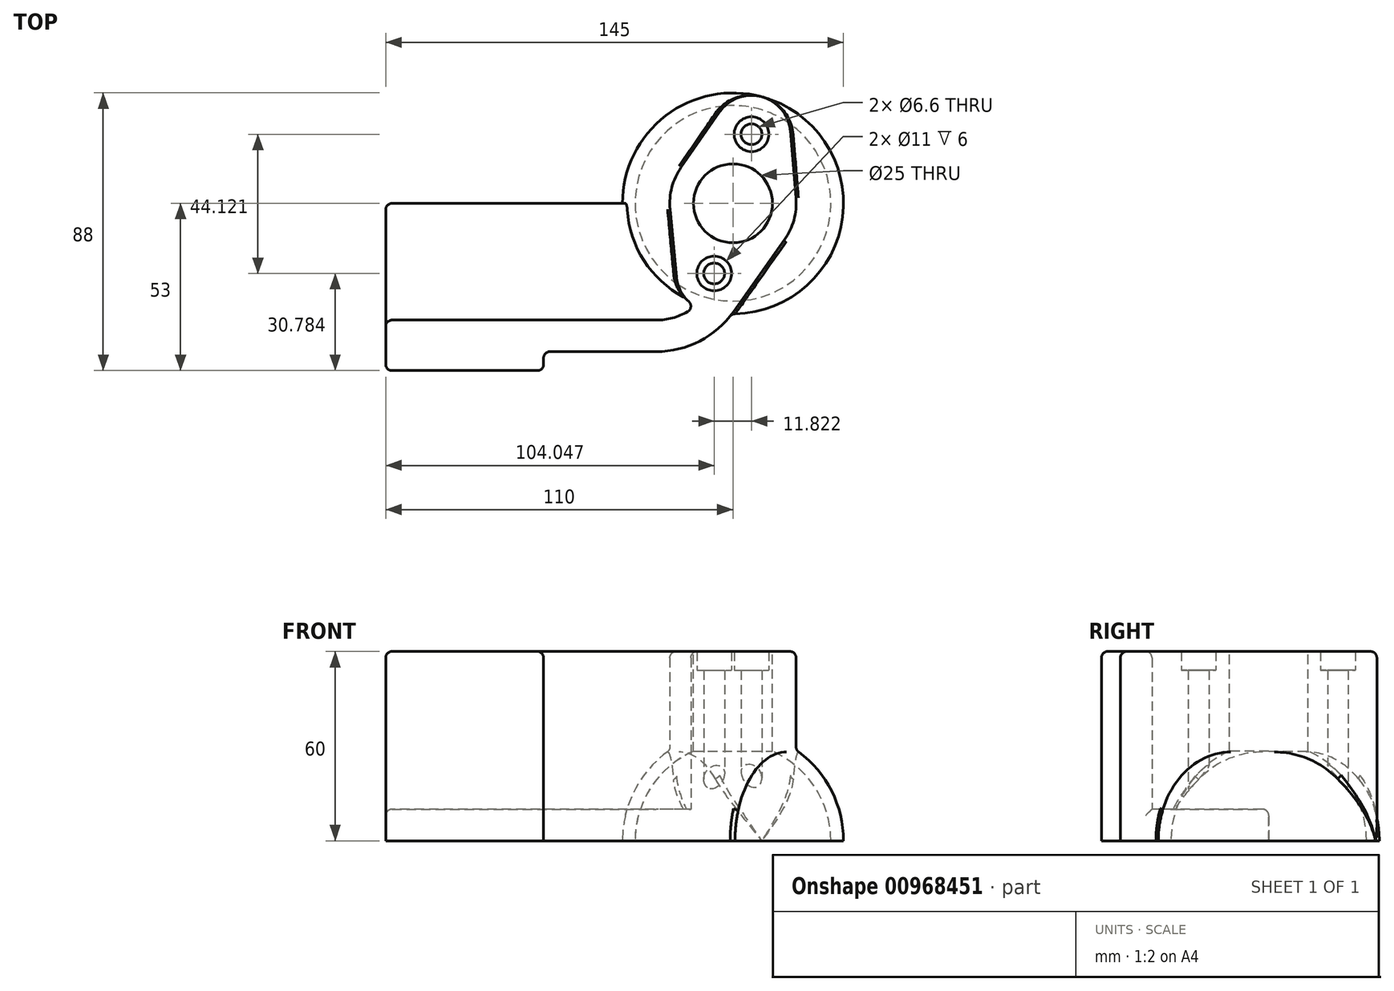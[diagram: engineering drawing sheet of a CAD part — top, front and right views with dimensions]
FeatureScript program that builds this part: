
annotation { "Feature Type Name" : "Feature", "Feature Type Description" : "" }
export const myFeature = defineFeature(function(context is Context, id is Id, definition is map)
    precondition{}
    {
        {
            var Q0;
            Q0=qCreatedBy(makeId("Top.planeOp"),FACE);
            var sketch = newSketch(context, id + "F0", { "sketchPlane" : qUnion([Q0])});
            skArc(sketch, "E0", {"start": v(-0.32, -35) * mm, "mid": v(6.97, 34.3) * mm, "end": v(-13.36, -32.35) * mm});
            skCircle(sketch, "E1", {"center": v(0, 0) * mm, "radius": 12.5 * mm, "construction": true});
            skLineSegment(sketch, "E2", {"start": v(9.06, 33.8) * mm, "end": v(-9.06, -33.8) * mm, "construction": true});
            skArc(sketch, "E3", {"start": v(-16.43, 11.41) * mm, "mid": v(-19.34, 5.08) * mm, "end": v(-19.91, -1.87) * mm});
            skArc(sketch, "E4", {"start": v(-17.9, -23.34) * mm, "mid": v(-16.68, -27.6) * mm, "end": v(-14, -31.12) * mm});
            skLineSegment(sketch, "E5", {"start": v(-4.25, 28.94) * mm, "end": v(-16.43, 11.41) * mm});
            skLineSegment(sketch, "E6", {"start": v(18.15, 22.93) * mm, "end": v(19.93, 1.67) * mm});
            skLineSegment(sketch, "E7", {"start": v(-17.9, -23.34) * mm, "end": v(-19.91, -1.87) * mm});
            skLineSegment(sketch, "E8", {"start": v(0.15, -34.36) * mm, "end": v(16.31, -11.57) * mm});
            skArc(sketch, "E9.trimOffspring", {"start": v(18.15, 22.93) * mm, "mid": v(9.06, 33.8) * mm, "end": v(-4.25, 28.94) * mm});
            skArc(sketch, "E10.trimOffspring", {"start": v(16.31, -11.57) * mm, "mid": v(19.3, -5.27) * mm, "end": v(19.93, 1.67) * mm});
            skPoint(sketch, "E11.orphan", {"position": v(20.07, 0) * mm});
            skPoint(sketch, "E12.orphan", {"position": v(-20.09, 0) * mm});
            skLineSegment(sketch, "E13", {"start": v(-34.3, -7) * mm, "end": v(-110, -7) * mm});
            skLineSegment(sketch, "E14", {"start": v(-110, -7) * mm, "end": v(-110, -53) * mm});
            skLineSegment(sketch, "E15", {"start": v(-110, -53) * mm, "end": v(-60, -53) * mm});
            skLineSegment(sketch, "E16", {"start": v(-60, -53) * mm, "end": v(-60, -47) * mm});
            skLineSegment(sketch, "E17", {"start": v(-60, -47) * mm, "end": v(-24.32, -47) * mm});
            skLineSegment(sketch, "E18", {"start": v(-110, -37) * mm, "end": v(-24.32, -37) * mm});
            skArc(sketch, "E19.filletArc", {"start": v(-24.32, -47) * mm, "mid": v(-10.55, -43.65) * mm, "end": v(0.15, -34.36) * mm});
            skArc(sketch, "E20", {"start": v(-24.32, -37) * mm, "mid": v(-19.16, -36.32) * mm, "end": v(-14.35, -34.33) * mm});
            skArc(sketch, "E21.filletArc", {"start": v(-14.35, -34.33) * mm, "mid": v(-13.35, -32.81) * mm, "end": v(-14, -31.12) * mm});
            skSolve(sketch);
        }
        {
            var Q0;
            Q0=qCreatedBy(makeId("Front.planeOp"),FACE);
            var sketch = newSketch(context, id + "F1", { "sketchPlane" : qUnion([Q0])});
            skArc(sketch, "E22", {"start": v(35, 0) * mm, "mid": v(24.75, 24.75) * mm, "end": v(0, 35) * mm});
            skPoint(sketch, "E23.orphan", {"position": v(0, 35) * mm});
            skLineSegment(sketch, "E24", {"start": v(0, 35) * mm, "end": v(0, 0) * mm});
            skLineSegment(sketch, "E25", {"start": v(0, 0) * mm, "end": v(35, 0) * mm});
            skSolve(sketch);
        }
        {
            var Q0;
            Q0=makeQuery(id+"F0.imprint","IMPRINT",FACE,{"disambiguationData":[TD([[makeQuery(id+"F0.imprint","IMPRINT",EDGE,{"derivedFrom":sQuery(id+"F0.wireOp",EDGE,"E3")}),1.0]])]});
            extrude(context, id + "F2", {"entities" : qUnion([Q0]), "depth" : 60 * mm, "offsetDistance" : 25 * mm});
        }
        {
            var Q0;
            Q0=makeQuery(id+"F1.imprint","IMPRINT",FACE,{"disambiguationData":[TD([[makeQuery(id+"F1.imprint","IMPRINT",EDGE,{"derivedFrom":sQuery(id+"F1.wireOp",EDGE,"E22")}),1.0]])]});
            var Q1;
            Q1=sQuery(id+"F1.wireOp",EDGE,"E24");
            revolve(context, id + "F3", {"operationType" : NewBodyOperationType.ADD, "surfaceOperationType" : NewSurfaceOperationType.NEW, "entities" : qUnion([Q0]), "axis" : qUnion([Q1]), "revolveType" : RevolveType.FULL});
        }
        {
            var Q0;
            Q0=makeQuery(id+"F2.opExtrude","SWEPT_FACE",FACE,{"disambiguationData":[OSD([sQuery(id+"F0.wireOp",EDGE,"E18")])]});
            var sketch = newSketch(context, id + "F4", { "sketchPlane" : qUnion([Q0])});
            skLineSegment(sketch, "E26.bottom", {"start": v(110, 0) * mm, "end": v(1.96, 0) * mm});
            skLineSegment(sketch, "E26.top", {"start": v(110, 10) * mm, "end": v(1.96, 10) * mm});
            skLineSegment(sketch, "E26.left", {"start": v(110, 0) * mm, "end": v(110, 10) * mm});
            skLineSegment(sketch, "E26.right", {"start": v(1.96, 0) * mm, "end": v(1.96, 10) * mm});
            skSolve(sketch);
        }
        {
            var Q0;
            Q0 = qSketchRegion(id + "F4", true);
            var Q1;
            Q1=qCreatedBy(makeId("Front.planeOp"),FACE);
            extrude(context, id + "F5", {"entities" : qUnion([Q0]), "operationType" : NewBodyOperationType.ADD, "endBound" : BoundingType.UP_TO_SURFACE, "depth" : 25 * mm, "endBoundEntityFace" : qUnion([Q1]), "offsetDistance" : 25 * mm});
        }
        {
            var Q0;
            Q0=makeQuery(id+"F3.boolean.opBoolean","INTERSECT",EDGE,{"derivedFrom":[makeQuery(id+"F2.opExtrude","SWEPT_FACE",FACE,{"disambiguationData":[OSD([sQuery(id+"F0.wireOp",EDGE,"E8")])]}),makeQuery(id+"F3.opRevolve","SWEPT_FACE",FACE,{"disambiguationData":[OSD([sQuery(id+"F1.wireOp",EDGE,"E22")])]})]});
            var Q1;
            Q1=makeQuery(id+"F3.boolean.opBoolean","INTERSECT",EDGE,{"derivedFrom":[makeQuery(id+"F2.opExtrude","SWEPT_FACE",FACE,{"disambiguationData":[OSD([sQuery(id+"F0.wireOp",EDGE,"E5")])]}),makeQuery(id+"F3.opRevolve","SWEPT_FACE",FACE,{"disambiguationData":[OSD([sQuery(id+"F1.wireOp",EDGE,"E22")])]})]});
            var Q2;
            Q2=makeQuery(id+"F5.opExtrude","CAP_EDGE",EDGE,{"disambiguationData":[OSD([sQuery(id+"F4.wireOp",EDGE,"E26.top")])],"isStart":false});
            var Q3;
            Q3=makeQuery(id+"F2.opExtrude","SWEPT_EDGE",EDGE,{"disambiguationData":[OSD([sQuery(id+"F0.wireOp",EDGE,"E16"),sQuery(id+"F0.wireOp",EDGE,"E17")])]});
            var Q4;
            Q4=makeQuery(id+"F2.opExtrude","SWEPT_EDGE",EDGE,{"disambiguationData":[OSD([sQuery(id+"F0.wireOp",EDGE,"E15"),sQuery(id+"F0.wireOp",EDGE,"E16")])]});
            var Q5;
            Q5=makeQuery(id+"F2.opExtrude","SWEPT_EDGE",EDGE,{"disambiguationData":[OSD([sQuery(id+"F0.wireOp",EDGE,"E14"),sQuery(id+"F0.wireOp",EDGE,"E15")])]});
            var Q6;
            Q6=makeQuery(id+"F2.opExtrude","SWEPT_EDGE",EDGE,{"disambiguationData":[OSD([sQuery(id+"F0.wireOp",EDGE,"E14"),sQuery(id+"F0.wireOp",EDGE,"E18")])]});
            fillet(context, id + "F6", {"entities" : qUnion([Q0, Q1, Q2, Q3, Q4, Q5, Q6]), "radius" : 2 * mm, "tangentPropagation" : true, "allowEdgeOverflow" : false});
        }
        {
            var Q0;
            Q0=makeQuery(id+"F5.opExtrude","SWEPT_EDGE",EDGE,{"disambiguationData":[OSD([sQuery(id+"F0.wireOp",EDGE,"E14"),sQuery(id+"F0.wireOp",EDGE,"E18"),sQuery(id+"F4.wireOp",EDGE,"E26.top"),sQuery(id+"F4.wireOp",EDGE,"E26.left")])]});
            fillet(context, id + "F7", {"entities" : qUnion([Q0]), "radius" : 2 * mm, "tangentPropagation" : true, "allowEdgeOverflow" : false});
        }
        {
            var Q0;
            Q0=makeQuery(id+"F2.opExtrude","CAP_FACE",FACE,{"disambiguationData":[OSD([sQuery(id+"F0.wireOp",EDGE,"E3"),sQuery(id+"F0.wireOp",EDGE,"E4"),sQuery(id+"F0.wireOp",EDGE,"E5"),sQuery(id+"F0.wireOp",EDGE,"E6"),sQuery(id+"F0.wireOp",EDGE,"E7"),sQuery(id+"F0.wireOp",EDGE,"E8"),sQuery(id+"F0.wireOp",EDGE,"E9.trimOffspring"),sQuery(id+"F0.wireOp",EDGE,"E10.trimOffspring"),sQuery(id+"F0.wireOp",EDGE,"E14"),sQuery(id+"F0.wireOp",EDGE,"E15"),sQuery(id+"F0.wireOp",EDGE,"E16"),sQuery(id+"F0.wireOp",EDGE,"E17"),sQuery(id+"F0.wireOp",EDGE,"E18"),sQuery(id+"F0.wireOp",EDGE,"E19.filletArc"),sQuery(id+"F0.wireOp",EDGE,"E20"),sQuery(id+"F0.wireOp",EDGE,"E21.filletArc")])],"isStart":false});
            var Q1;
            Q1=makeQuery(id+"F5.opExtrude","CAP_EDGE",EDGE,{"disambiguationData":[OSD([sQuery(id+"F4.wireOp",EDGE,"E26.top")])],"isStart":true});
            fillet(context, id + "F8", {"entities" : qUnion([Q0, Q1]), "radius" : 2 * mm, "tangentPropagation" : true, "allowEdgeOverflow" : false});
        }
        {
            var Q0;
            Q0=qCreatedBy(makeId("Front.planeOp"),FACE);
            var sketch = newSketch(context, id + "F9", { "sketchPlane" : qUnion([Q0])});
            skLineSegment(sketch, "E27.0", {"start": v(0, 35) * mm, "end": v(0, 0) * mm});
            skLineSegment(sketch, "E27.1", {"start": v(0, 0) * mm, "end": v(35, 0) * mm});
            skArc(sketch, "E28", {"start": v(31, 0) * mm, "mid": v(21.92, 21.92) * mm, "end": v(0, 31) * mm});
            skSolve(sketch);
        }
        {
            var Q0;
            Q0 = qSketchRegion(id + "F9", true);
            var Q1;
            Q1=sQuery(id+"F9.wireOp",EDGE,"E27.0");
            revolve(context, id + "F10", {"operationType" : NewBodyOperationType.REMOVE, "surfaceOperationType" : NewSurfaceOperationType.NEW, "entities" : qUnion([Q0]), "axis" : qUnion([Q1]), "revolveType" : RevolveType.FULL, "oppositeDirection" : true});
        }
        {
            var Q0;
            Q0=makeQuery(id+"F2.opExtrude","CAP_FACE",FACE,{"disambiguationData":[OSD([sQuery(id+"F0.wireOp",EDGE,"E3"),sQuery(id+"F0.wireOp",EDGE,"E4"),sQuery(id+"F0.wireOp",EDGE,"E5"),sQuery(id+"F0.wireOp",EDGE,"E6"),sQuery(id+"F0.wireOp",EDGE,"E7"),sQuery(id+"F0.wireOp",EDGE,"E8"),sQuery(id+"F0.wireOp",EDGE,"E9.trimOffspring"),sQuery(id+"F0.wireOp",EDGE,"E10.trimOffspring"),sQuery(id+"F0.wireOp",EDGE,"E14"),sQuery(id+"F0.wireOp",EDGE,"E15"),sQuery(id+"F0.wireOp",EDGE,"E16"),sQuery(id+"F0.wireOp",EDGE,"E17"),sQuery(id+"F0.wireOp",EDGE,"E18"),sQuery(id+"F0.wireOp",EDGE,"E19.filletArc"),sQuery(id+"F0.wireOp",EDGE,"E20"),sQuery(id+"F0.wireOp",EDGE,"E21.filletArc")])],"isStart":false});
            var sketch = newSketch(context, id + "F11", { "sketchPlane" : qUnion([Q0])});
            skCircle(sketch, "E29.0", {"center": v(0, 0) * mm, "radius": 12.5 * mm});
            skSolve(sketch);
        }
        {
            var Q0;
            Q0=makeQuery(id+"F11.imprint","IMPRINT",FACE,{"disambiguationData":[TD([[makeQuery(id+"F11.imprint","IMPRINT",EDGE,{"derivedFrom":sQuery(id+"F11.wireOp",EDGE,"E29.0")}),1.0]])]});
            extrude(context, id + "F12", {"entities" : qUnion([Q0]), "operationType" : NewBodyOperationType.REMOVE, "endBound" : BoundingType.THROUGH_ALL, "oppositeDirection" : true, "depth" : 25 * mm, "offsetDistance" : 25 * mm});
        }
        {
            var Q0;
            Q0=makeQuery(id+"F2.opExtrude","CAP_FACE",FACE,{"disambiguationData":[OSD([sQuery(id+"F0.wireOp",EDGE,"E3"),sQuery(id+"F0.wireOp",EDGE,"E4"),sQuery(id+"F0.wireOp",EDGE,"E5"),sQuery(id+"F0.wireOp",EDGE,"E6"),sQuery(id+"F0.wireOp",EDGE,"E7"),sQuery(id+"F0.wireOp",EDGE,"E8"),sQuery(id+"F0.wireOp",EDGE,"E9.trimOffspring"),sQuery(id+"F0.wireOp",EDGE,"E10.trimOffspring"),sQuery(id+"F0.wireOp",EDGE,"E14"),sQuery(id+"F0.wireOp",EDGE,"E15"),sQuery(id+"F0.wireOp",EDGE,"E16"),sQuery(id+"F0.wireOp",EDGE,"E17"),sQuery(id+"F0.wireOp",EDGE,"E18"),sQuery(id+"F0.wireOp",EDGE,"E19.filletArc"),sQuery(id+"F0.wireOp",EDGE,"E20"),sQuery(id+"F0.wireOp",EDGE,"E21.filletArc")])],"isStart":false});
            var sketch = newSketch(context, id + "F13", { "sketchPlane" : qUnion([Q0])});
            skPoint(sketch, "E30.0", {"position": v(5.87, 21.9) * mm});
            skPoint(sketch, "E30.1", {"position": v(-5.95, -22.22) * mm});
            skSolve(sketch);
        }
        {
            var Q0;
            Q0=sQuery(id+"F13.wireOp",VERTEX,"E30.0");
            var Q1;
            Q1=sQuery(id+"F13.wireOp",VERTEX,"E30.1");
            var Q2;
            Q2=makeQuery(id+"F2.opExtrude","SWEPT_BODY",BODY,{"disambiguationData":[OSD([sQuery(id+"F0.wireOp",EDGE,"E3"),sQuery(id+"F0.wireOp",EDGE,"E4"),sQuery(id+"F0.wireOp",EDGE,"E5"),sQuery(id+"F0.wireOp",EDGE,"E6"),sQuery(id+"F0.wireOp",EDGE,"E7"),sQuery(id+"F0.wireOp",EDGE,"E8"),sQuery(id+"F0.wireOp",EDGE,"E9.trimOffspring"),sQuery(id+"F0.wireOp",EDGE,"E10.trimOffspring"),sQuery(id+"F0.wireOp",EDGE,"E14"),sQuery(id+"F0.wireOp",EDGE,"E15"),sQuery(id+"F0.wireOp",EDGE,"E16"),sQuery(id+"F0.wireOp",EDGE,"E17"),sQuery(id+"F0.wireOp",EDGE,"E18"),sQuery(id+"F0.wireOp",EDGE,"E19.filletArc"),sQuery(id+"F0.wireOp",EDGE,"E20"),sQuery(id+"F0.wireOp",EDGE,"E21.filletArc")])]});
            hole(context, id + "F14", {"style" : HoleStyle.C_BORE, "endStyle" : HoleEndStyle.THROUGH, "holeDiameter" : 6.6 * mm, "cBoreDiameter" : 11 * mm, "cBoreDepth" : 6 * mm, "majorDiameter" : 8 * mm, "isTappedThrough" : true, "tappedDepth" : 8.25 * mm, "tapClearance" : 3, "startFromSketch" : true, "locations" : qUnion([Q0, Q1]), "scope" : qUnion([Q2])});
        }
    });
